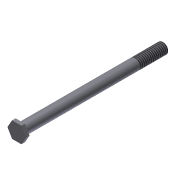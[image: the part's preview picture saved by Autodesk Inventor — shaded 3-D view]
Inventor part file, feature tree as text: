
AUTODESK INVENTOR PART (.ipt)
format: ipt  version: 2011 (Build 150239000, 239)  size: 89,088 bytes
history: native  units: in
note: dims shown in document units (in); Inventor stores cm internally (conversion verified against a paired STEP export)
features: extrude x2, sketch x2, thread x1, chamfer x1
ambient origin geometry x8: Origin, YZ Plane, XZ Plane, XY Plane, X Axis, Y Axis, Z Axis, Center Point
bodies: Solid1 (feature_tree)
feature tree (6):
  extrude  "Extrusion1"  Depth=5.0in TaperAngle=0.0deg
  extrude  "Extrusion2"  Depth=0.125in TaperAngle=0.0deg
  thread  "Thread1"  [1 undecoded]
  chamfer  "Chamfer1"  Distance=0.02in Angle=45.0deg
  sketch  "Sketch1"  dims[d0=0.375in d1=5.0in d2=0.0in]
  sketch  "Sketch2"  dims[d3=0.5625in d4=0.125in d5=0.0in d6=1.0in d7=0.0in d8=0.02in d9=0.125in d10=45.0deg]
note: 1 required parameter value undecoded (feature->parameter linkage not recoverable at this tier; creation-order binding heuristic only, values carry confidence <= 0.55)
